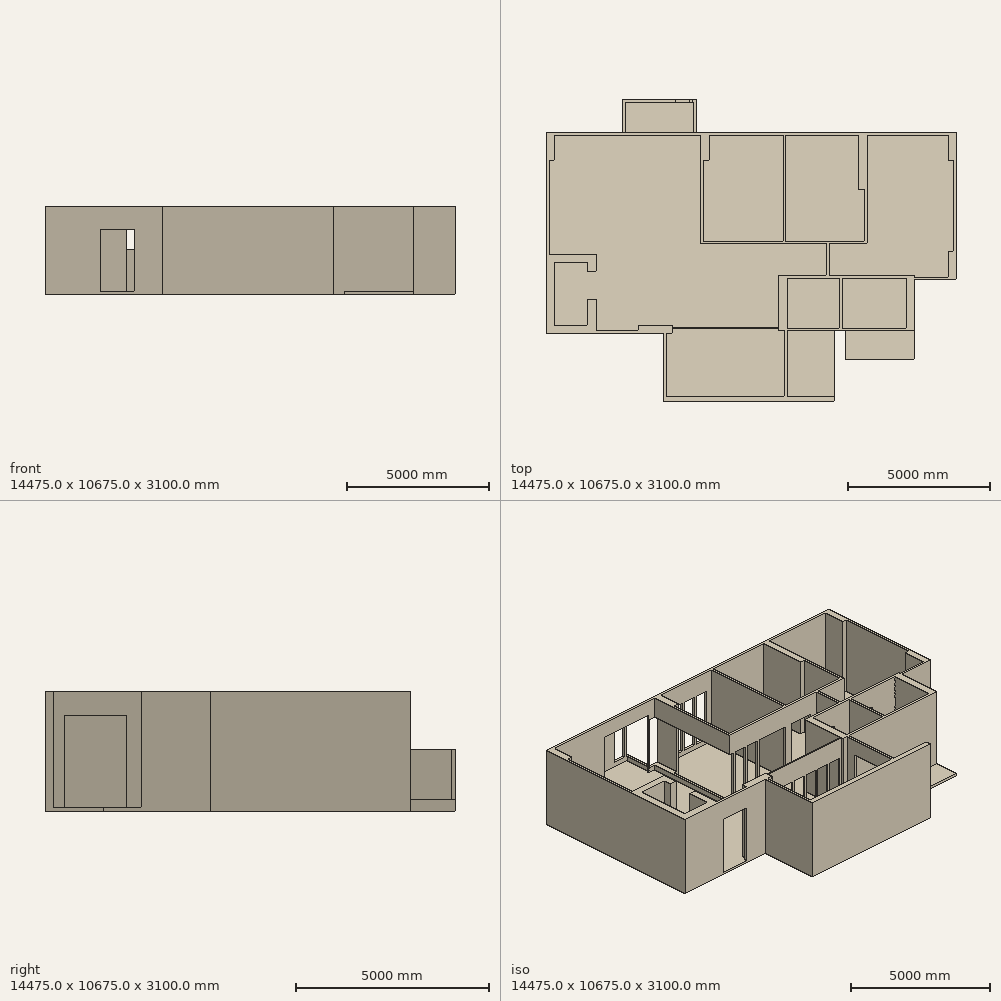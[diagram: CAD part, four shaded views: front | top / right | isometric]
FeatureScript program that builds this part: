
annotation { "Feature Type Name" : "Feature", "Feature Type Description" : "" }
export const myFeature = defineFeature(function(context is Context, id is Id, definition is map)
    precondition{}
    {
        {
            var Q0;
            Q0=qCreatedBy(makeId("Top.planeOp"),FACE);
            var sketch = newSketch(context, id + "F0", { "sketchPlane" : qUnion([Q0])});
            skLineSegment(sketch, "E0", {"start": v(0, 0) * mm, "end": v(-4125, 0) * mm});
            skLineSegment(sketch, "E1", {"start": v(-4125, 0) * mm, "end": v(-4125, 7100) * mm});
            skLineSegment(sketch, "E2", {"start": v(-4125, 7100) * mm, "end": v(-1425, 7100) * mm});
            skLineSegment(sketch, "E3", {"start": v(-1425, 7100) * mm, "end": v(-1425, 8275) * mm});
            skLineSegment(sketch, "E4", {"start": v(-1425, 8275) * mm, "end": v(1175, 8275) * mm});
            skLineSegment(sketch, "E5", {"start": v(1175, 8275) * mm, "end": v(1175, 7100) * mm});
            skLineSegment(sketch, "E6", {"start": v(1175, 7100) * mm, "end": v(10350, 7100) * mm});
            skLineSegment(sketch, "E7", {"start": v(10350, 7100) * mm, "end": v(10350, 1900) * mm});
            skLineSegment(sketch, "E8", {"start": v(10350, 1900) * mm, "end": v(8875, 1900) * mm});
            skLineSegment(sketch, "E9", {"start": v(8875, 1900) * mm, "end": v(8875, -900) * mm});
            skLineSegment(sketch, "E10", {"start": v(8875, -900) * mm, "end": v(6425, -900) * mm});
            skLineSegment(sketch, "E11", {"start": v(6050, -900) * mm, "end": v(6050, -2400) * mm});
            skLineSegment(sketch, "E12", {"start": v(6050, -2400) * mm, "end": v(0, -2400) * mm});
            skLineSegment(sketch, "E13", {"start": v(0, -2400) * mm, "end": v(0, 0) * mm});
            skLineSegment(sketch, "E14", {"start": v(6425, -900) * mm, "end": v(6425, 0) * mm});
            skLineSegment(sketch, "E15", {"start": v(6050, 0) * mm, "end": v(6050, -900) * mm});
            skLineSegment(sketch, "E16", {"start": v(6050, 0) * mm, "end": v(6050, 100) * mm});
            skLineSegment(sketch, "E17", {"start": v(6050, 100) * mm, "end": v(6425, 100) * mm});
            skLineSegment(sketch, "E18", {"start": v(6425, 100) * mm, "end": v(6425, 0) * mm});
            skSolve(sketch);
        }
        {
            var Q0;
            Q0=qSketchRegion(id+"F0",true);
            extrude(context, id + "F1", {"entities" : qUnion([Q0]), "oppositeDirection" : true, "depth" : 100 * mm});
        }
        {
            var Q0;
            Q0=makeQuery(id+"F1.opExtrude","CAP_FACE",FACE,{"disambiguationData":[OSD([sQuery(id+"F0.wireOp",EDGE,"E0"),sQuery(id+"F0.wireOp",EDGE,"E1"),sQuery(id+"F0.wireOp",EDGE,"E2"),sQuery(id+"F0.wireOp",EDGE,"E3"),sQuery(id+"F0.wireOp",EDGE,"E4"),sQuery(id+"F0.wireOp",EDGE,"E5"),sQuery(id+"F0.wireOp",EDGE,"E6"),sQuery(id+"F0.wireOp",EDGE,"E7"),sQuery(id+"F0.wireOp",EDGE,"E8"),sQuery(id+"F0.wireOp",EDGE,"E9"),sQuery(id+"F0.wireOp",EDGE,"E10"),sQuery(id+"F0.wireOp",EDGE,"E11"),sQuery(id+"F0.wireOp",EDGE,"E12"),sQuery(id+"F0.wireOp",EDGE,"E13"),sQuery(id+"F0.wireOp",EDGE,"E14"),sQuery(id+"F0.wireOp",EDGE,"EO6Hl1aY-iN83-L0no-XnAw-wlp1sX6jhs91"),sQuery(id+"F0.wireOp",EDGE,"E15")])],"isStart":true});
            var sketch = newSketch(context, id + "F2", { "sketchPlane" : qUnion([Q0])});
            skLineSegment(sketch, "E19", {"start": v(-4125, 0) * mm, "end": v(-4125, 2800) * mm});
            skLineSegment(sketch, "E20", {"start": v(-4125, 2800) * mm, "end": v(-2375, 2800) * mm});
            skLineSegment(sketch, "E21", {"start": v(-2375, 2800) * mm, "end": v(-2375, 2200) * mm});
            skLineSegment(sketch, "E22", {"start": v(-2375, 2200) * mm, "end": v(-2675, 2200) * mm});
            skLineSegment(sketch, "E23", {"start": v(-2675, 2200) * mm, "end": v(-2675, 2500) * mm});
            skLineSegment(sketch, "E24", {"start": v(-2675, 2500) * mm, "end": v(-3825, 2500) * mm});
            skLineSegment(sketch, "E25", {"start": v(-3825, 2500) * mm, "end": v(-3825, 300) * mm});
            skLineSegment(sketch, "E26", {"start": v(-3825, 300) * mm, "end": v(-2675, 300) * mm});
            skLineSegment(sketch, "E27", {"start": v(-2675, 300) * mm, "end": v(-2675, 1200) * mm});
            skLineSegment(sketch, "E28", {"start": v(-2675, 1200) * mm, "end": v(-2375, 1200) * mm});
            skLineSegment(sketch, "E29", {"start": v(-2375, 1200) * mm, "end": v(-2375, 0) * mm});
            skLineSegment(sketch, "E30", {"start": v(-2375, 0) * mm, "end": v(-4125, 0) * mm});
            skSolve(sketch);
        }
        {
            var Q0;
            Q0=qSketchRegion(id+"F2",true);
            extrude(context, id + "F3", {"entities" : qUnion([Q0]), "operationType" : NewBodyOperationType.ADD, "depth" : 3000 * mm});
        }
        {
            var Q0;
            Q0=makeQuery(id+"F1.opExtrude","CAP_FACE",FACE,{"disambiguationData":[OSD([sQuery(id+"F0.wireOp",EDGE,"E0"),sQuery(id+"F0.wireOp",EDGE,"E1"),sQuery(id+"F0.wireOp",EDGE,"E2"),sQuery(id+"F0.wireOp",EDGE,"E3"),sQuery(id+"F0.wireOp",EDGE,"E4"),sQuery(id+"F0.wireOp",EDGE,"E5"),sQuery(id+"F0.wireOp",EDGE,"E6"),sQuery(id+"F0.wireOp",EDGE,"E7"),sQuery(id+"F0.wireOp",EDGE,"E8"),sQuery(id+"F0.wireOp",EDGE,"E9"),sQuery(id+"F0.wireOp",EDGE,"E10"),sQuery(id+"F0.wireOp",EDGE,"E11"),sQuery(id+"F0.wireOp",EDGE,"E12"),sQuery(id+"F0.wireOp",EDGE,"E13"),sQuery(id+"F0.wireOp",EDGE,"E14"),sQuery(id+"F0.wireOp",EDGE,"EO6Hl1aY-iN83-L0no-XnAw-wlp1sX6jhs91"),sQuery(id+"F0.wireOp",EDGE,"E15")])],"isStart":true});
            var sketch = newSketch(context, id + "F4", { "sketchPlane" : qUnion([Q0])});
            skLineSegment(sketch, "E31.bottom", {"start": v(-4125, 7100) * mm, "end": v(-3825, 7100) * mm});
            skLineSegment(sketch, "E31.top", {"start": v(-4125, 6100) * mm, "end": v(-3825, 6100) * mm});
            skLineSegment(sketch, "E31.left", {"start": v(-4125, 7100) * mm, "end": v(-4125, 6100) * mm});
            skLineSegment(sketch, "E31.right", {"start": v(-3825, 7100) * mm, "end": v(-3825, 6100) * mm});
            skLineSegment(sketch, "E32.bottom", {"start": v(1325, 7100) * mm, "end": v(1625, 7100) * mm});
            skLineSegment(sketch, "E32.top", {"start": v(1325, 6100) * mm, "end": v(1625, 6100) * mm});
            skLineSegment(sketch, "E32.left", {"start": v(1325, 7100) * mm, "end": v(1325, 6100) * mm});
            skLineSegment(sketch, "E32.right", {"start": v(1625, 7100) * mm, "end": v(1625, 6100) * mm});
            skLineSegment(sketch, "E33.bottom", {"start": v(6900, 7100) * mm, "end": v(7200, 7100) * mm});
            skLineSegment(sketch, "E33.top", {"start": v(6900, 5100) * mm, "end": v(7200, 5100) * mm});
            skLineSegment(sketch, "E33.left", {"start": v(6900, 7100) * mm, "end": v(6900, 5100) * mm});
            skLineSegment(sketch, "E33.right", {"start": v(7200, 7100) * mm, "end": v(7200, 5100) * mm});
            skLineSegment(sketch, "E34.bottom", {"start": v(10350, 7100) * mm, "end": v(10050, 7100) * mm});
            skLineSegment(sketch, "E34.top", {"start": v(10350, 6100) * mm, "end": v(10050, 6100) * mm});
            skLineSegment(sketch, "E34.left", {"start": v(10350, 7100) * mm, "end": v(10350, 6100) * mm});
            skLineSegment(sketch, "E34.right", {"start": v(10050, 7100) * mm, "end": v(10050, 6100) * mm});
            skLineSegment(sketch, "E35.bottom", {"start": v(10350, 1900) * mm, "end": v(10050, 1900) * mm});
            skLineSegment(sketch, "E35.top", {"start": v(10350, 2900) * mm, "end": v(10050, 2900) * mm});
            skLineSegment(sketch, "E35.left", {"start": v(10350, 1900) * mm, "end": v(10350, 2900) * mm});
            skLineSegment(sketch, "E35.right", {"start": v(10050, 1900) * mm, "end": v(10050, 2900) * mm});
            skLineSegment(sketch, "E36.bottom", {"start": v(8875, 2050) * mm, "end": v(8575, 2050) * mm});
            skLineSegment(sketch, "E36.top", {"start": v(8875, 100) * mm, "end": v(8575, 100) * mm});
            skLineSegment(sketch, "E36.left", {"start": v(8875, 2050) * mm, "end": v(8875, 100) * mm});
            skLineSegment(sketch, "E36.right", {"start": v(8575, 2050) * mm, "end": v(8575, 100) * mm});
            skLineSegment(sketch, "E37.bottom", {"start": v(4375, 2050) * mm, "end": v(4075, 2050) * mm});
            skLineSegment(sketch, "E37.top", {"start": v(4375, 100) * mm, "end": v(4075, 100) * mm});
            skLineSegment(sketch, "E37.left", {"start": v(4375, 2050) * mm, "end": v(4375, 100) * mm});
            skLineSegment(sketch, "E37.right", {"start": v(4075, 2050) * mm, "end": v(4075, 100) * mm});
            skLineSegment(sketch, "E38.bottom", {"start": v(325, 0) * mm, "end": v(-875, 0) * mm});
            skLineSegment(sketch, "E38.top", {"start": v(325, 300) * mm, "end": v(-875, 300) * mm});
            skLineSegment(sketch, "E38.left", {"start": v(325, 0) * mm, "end": v(325, 300) * mm});
            skLineSegment(sketch, "E38.right", {"start": v(-875, 0) * mm, "end": v(-875, 300) * mm});
            skLineSegment(sketch, "E39.bottom", {"start": v(0, -2400) * mm, "end": v(6050, -2400) * mm});
            skLineSegment(sketch, "E39.top", {"start": v(0, -2200) * mm, "end": v(6050, -2200) * mm});
            skLineSegment(sketch, "E39.left", {"start": v(0, -2400) * mm, "end": v(0, -2200) * mm});
            skLineSegment(sketch, "E39.right", {"start": v(6050, -2400) * mm, "end": v(6050, -2200) * mm});
            skSolve(sketch);
        }
        {
            var Q0;
            Q0=qSketchRegion(id+"F4",true);
            extrude(context, id + "F5", {"entities" : qUnion([Q0]), "operationType" : NewBodyOperationType.ADD, "depth" : 3000 * mm});
        }
        {
            var Q0;
            Q0=makeQuery(id+"F1.opExtrude","CAP_FACE",FACE,{"disambiguationData":[OSD([sQuery(id+"F0.wireOp",EDGE,"E0"),sQuery(id+"F0.wireOp",EDGE,"E1"),sQuery(id+"F0.wireOp",EDGE,"E2"),sQuery(id+"F0.wireOp",EDGE,"E3"),sQuery(id+"F0.wireOp",EDGE,"E4"),sQuery(id+"F0.wireOp",EDGE,"E5"),sQuery(id+"F0.wireOp",EDGE,"E6"),sQuery(id+"F0.wireOp",EDGE,"E7"),sQuery(id+"F0.wireOp",EDGE,"E8"),sQuery(id+"F0.wireOp",EDGE,"E9"),sQuery(id+"F0.wireOp",EDGE,"E10"),sQuery(id+"F0.wireOp",EDGE,"E11"),sQuery(id+"F0.wireOp",EDGE,"E12"),sQuery(id+"F0.wireOp",EDGE,"E13"),sQuery(id+"F0.wireOp",EDGE,"E14"),sQuery(id+"F0.wireOp",EDGE,"EO6Hl1aY-iN83-L0no-XnAw-wlp1sX6jhs91"),sQuery(id+"F0.wireOp",EDGE,"E15")])],"isStart":true});
            var sketch = newSketch(context, id + "F6", { "sketchPlane" : qUnion([Q0])});
            skLineSegment(sketch, "E40", {"start": v(0, -2200) * mm, "end": v(0, 0) * mm});
            skLineSegment(sketch, "E41", {"start": v(0, 0) * mm, "end": v(-4125, 0) * mm});
            skLineSegment(sketch, "E42", {"start": v(-4125, 0) * mm, "end": v(-4125, 7100) * mm});
            skLineSegment(sketch, "E43", {"start": v(-4125, 7100) * mm, "end": v(-1425, 7100) * mm});
            skLineSegment(sketch, "E44", {"start": v(-1425, 7100) * mm, "end": v(-1425, 7000) * mm});
            skLineSegment(sketch, "E45", {"start": v(-1425, 7000) * mm, "end": v(-4025, 7000) * mm});
            skLineSegment(sketch, "E46", {"start": v(-4025, 7000) * mm, "end": v(-4025, 100) * mm});
            skLineSegment(sketch, "E47", {"start": v(-4025, 100) * mm, "end": v(100, 100) * mm});
            skLineSegment(sketch, "E48", {"start": v(100, 100) * mm, "end": v(100, -2200) * mm});
            skLineSegment(sketch, "E49", {"start": v(100, -2200) * mm, "end": v(0, -2200) * mm});
            skLineSegment(sketch, "E50.bottom", {"start": v(-1425, 7100) * mm, "end": v(1325, 7100) * mm});
            skLineSegment(sketch, "E50.top", {"start": v(-1425, 7000) * mm, "end": v(1325, 7000) * mm});
            skLineSegment(sketch, "E50.right", {"start": v(1325, 7100) * mm, "end": v(1325, 7000) * mm});
            skSolve(sketch);
        }
        {
            var Q0;
            Q0=qSketchRegion(id+"F6",true);
            extrude(context, id + "F7", {"entities" : qUnion([Q0]), "depth" : 3000 * mm});
        }
        {
            var Q0;
            Q0=makeQuery(id+"F1.opExtrude","CAP_FACE",FACE,{"disambiguationData":[OSD([sQuery(id+"F0.wireOp",EDGE,"E0"),sQuery(id+"F0.wireOp",EDGE,"E1"),sQuery(id+"F0.wireOp",EDGE,"E2"),sQuery(id+"F0.wireOp",EDGE,"E3"),sQuery(id+"F0.wireOp",EDGE,"E4"),sQuery(id+"F0.wireOp",EDGE,"E5"),sQuery(id+"F0.wireOp",EDGE,"E6"),sQuery(id+"F0.wireOp",EDGE,"E7"),sQuery(id+"F0.wireOp",EDGE,"E8"),sQuery(id+"F0.wireOp",EDGE,"E9"),sQuery(id+"F0.wireOp",EDGE,"E10"),sQuery(id+"F0.wireOp",EDGE,"E11"),sQuery(id+"F0.wireOp",EDGE,"E12"),sQuery(id+"F0.wireOp",EDGE,"E13"),sQuery(id+"F0.wireOp",EDGE,"E14"),sQuery(id+"F0.wireOp",EDGE,"EO6Hl1aY-iN83-L0no-XnAw-wlp1sX6jhs91"),sQuery(id+"F0.wireOp",EDGE,"E15")])],"isStart":true});
            var sketch = newSketch(context, id + "F8", { "sketchPlane" : qUnion([Q0])});
            skLineSegment(sketch, "E51", {"start": v(7200, 3170) * mm, "end": v(7200, 7100) * mm});
            skLineSegment(sketch, "E52", {"start": v(7200, 7100) * mm, "end": v(1325, 7100) * mm});
            skLineSegment(sketch, "E53", {"start": v(1325, 7100) * mm, "end": v(1325, 3170) * mm});
            skLineSegment(sketch, "E54", {"start": v(1325, 3170) * mm, "end": v(5775, 3170) * mm});
            skLineSegment(sketch, "E55.bottom", {"start": v(1425, 3270) * mm, "end": v(4225, 3270) * mm});
            skLineSegment(sketch, "E55.top", {"start": v(1425, 7000) * mm, "end": v(4225, 7000) * mm});
            skLineSegment(sketch, "E55.left", {"start": v(1425, 3270) * mm, "end": v(1425, 7000) * mm});
            skLineSegment(sketch, "E55.right", {"start": v(4225, 3270) * mm, "end": v(4225, 7000) * mm});
            skLineSegment(sketch, "E56.bottom", {"start": v(4325, 7000) * mm, "end": v(7100, 7000) * mm});
            skLineSegment(sketch, "E56.top", {"start": v(4325, 3270) * mm, "end": v(7100, 3270) * mm});
            skLineSegment(sketch, "E56.left", {"start": v(4325, 7000) * mm, "end": v(4325, 3270) * mm});
            skLineSegment(sketch, "E56.right", {"start": v(7100, 7000) * mm, "end": v(7100, 3270) * mm});
            skLineSegment(sketch, "E57.bottom", {"start": v(7200, 7100) * mm, "end": v(10350, 7100) * mm});
            skLineSegment(sketch, "E57.top", {"start": v(7200, 7000) * mm, "end": v(10250, 7000) * mm});
            skLineSegment(sketch, "E57.left", {"start": v(7200, 7100) * mm, "end": v(7200, 7000) * mm});
            skLineSegment(sketch, "E57.right", {"start": v(10350, 7100) * mm, "end": v(10350, 7000) * mm});
            skLineSegment(sketch, "E58.bottom", {"start": v(10350, 7100) * mm, "end": v(10250, 7100) * mm});
            skLineSegment(sketch, "E58.top", {"start": v(10350, 1900) * mm, "end": v(10250, 1900) * mm});
            skLineSegment(sketch, "E58.left", {"start": v(10350, 7100) * mm, "end": v(10350, 1900) * mm});
            skLineSegment(sketch, "E58.right", {"start": v(10250, 7000) * mm, "end": v(10250, 1975) * mm});
            skPoint(sketch, "E59.oppositeSnap0", {"position": v(8875, 1975) * mm});
            skLineSegment(sketch, "E59.bottom", {"start": v(10250, 1900) * mm, "end": v(8875, 1900) * mm});
            skLineSegment(sketch, "E59.top", {"start": v(10250, 1975) * mm, "end": v(8875, 1975) * mm});
            skLineSegment(sketch, "E59.right", {"start": v(8875, 1900) * mm, "end": v(8875, 1975) * mm});
            skLineSegment(sketch, "E60.bottom", {"start": v(8575, 2050) * mm, "end": v(5875, 2050) * mm});
            skLineSegment(sketch, "E60.top", {"start": v(8575, 1950) * mm, "end": v(6325, 1950) * mm});
            skLineSegment(sketch, "E60.left", {"start": v(8575, 2050) * mm, "end": v(8575, 1950) * mm});
            skLineSegment(sketch, "E60.right", {"start": v(4375, 2050) * mm, "end": v(4375, 1950) * mm});
            skLineSegment(sketch, "E61.bottom", {"start": v(4375, 100) * mm, "end": v(8575, 100) * mm});
            skLineSegment(sketch, "E61.top", {"start": v(4375, 200) * mm, "end": v(6225, 200) * mm});
            skLineSegment(sketch, "E61.left", {"start": v(4375, 100) * mm, "end": v(4375, 200) * mm});
            skLineSegment(sketch, "E61.right", {"start": v(8575, 100) * mm, "end": v(8575, 200) * mm});
            skLineSegment(sketch, "E62.left", {"start": v(6225, 1950) * mm, "end": v(6225, 200) * mm});
            skLineSegment(sketch, "E62.right", {"start": v(6325, 1950) * mm, "end": v(6325, 200) * mm});
            skLineSegment(sketch, "E63.trimOffspring", {"start": v(6225, 1950) * mm, "end": v(4375, 1950) * mm});
            skLineSegment(sketch, "E64.trimOffspring", {"start": v(6325, 200) * mm, "end": v(8575, 200) * mm});
            skLineSegment(sketch, "E65.left", {"start": v(5775, 3170) * mm, "end": v(5775, 2050) * mm});
            skLineSegment(sketch, "E65.right", {"start": v(5875, 3170) * mm, "end": v(5875, 2050) * mm});
            skLineSegment(sketch, "E66.trimOffspring", {"start": v(5875, 3170) * mm, "end": v(7200, 3170) * mm});
            skLineSegment(sketch, "E67.trimOffspring", {"start": v(5775, 2050) * mm, "end": v(4375, 2050) * mm});
            skLineSegment(sketch, "E68.bottom", {"start": v(4375, 200) * mm, "end": v(4275, 200) * mm});
            skLineSegment(sketch, "E68.top", {"start": v(4375, -2400) * mm, "end": v(4275, -2400) * mm});
            skLineSegment(sketch, "E68.left", {"start": v(4375, 200) * mm, "end": v(4375, -2400) * mm});
            skLineSegment(sketch, "E68.right", {"start": v(4275, 200) * mm, "end": v(4275, -2400) * mm});
            skSolve(sketch);
        }
        {
            var Q0;
            Q0=qSketchRegion(id+"F8",true);
            extrude(context, id + "F9", {"entities" : qUnion([Q0]), "operationType" : NewBodyOperationType.ADD, "depth" : 3000 * mm});
        }
        {
            var Q0;
            Q0=makeQuery(id+"F7.opExtrude","SWEPT_FACE",FACE,{"disambiguationData":[OSD([sQuery(id+"F6.wireOp",EDGE,"E41")])]});
            var sketch = newSketch(context, id + "F10", { "sketchPlane" : qUnion([Q0])});
            skLineSegment(sketch, "E69.bottom", {"start": v(-975, 0) * mm, "end": v(-2175, 0) * mm});
            skLineSegment(sketch, "E69.top", {"start": v(-975, 2200) * mm, "end": v(-2175, 2200) * mm});
            skLineSegment(sketch, "E69.left", {"start": v(-975, 0) * mm, "end": v(-975, 2200) * mm});
            skLineSegment(sketch, "E69.right", {"start": v(-2175, 0) * mm, "end": v(-2175, 2200) * mm});
            skSolve(sketch);
        }
        {
            var Q0;
            Q0=qSketchRegion(id+"F10",true);
            extrude(context, id + "F11", {"entities" : qUnion([Q0]), "operationType" : NewBodyOperationType.REMOVE, "oppositeDirection" : true, "depth" : 100 * mm});
        }
        {
            var Q0;
            Q0=makeQuery(id+"F9.opExtrude","SWEPT_FACE",FACE,{"disambiguationData":[OSD([sQuery(id+"F8.wireOp",EDGE,"E54")])]});
            var sketch = newSketch(context, id + "F12", { "sketchPlane" : qUnion([Q0])});
            skLineSegment(sketch, "E70.bottom", {"start": v(3175, 2200) * mm, "end": v(4175, 2200) * mm});
            skLineSegment(sketch, "E70.top", {"start": v(3175, 0) * mm, "end": v(4175, 0) * mm});
            skLineSegment(sketch, "E70.left", {"start": v(3175, 2200) * mm, "end": v(3175, 0) * mm});
            skLineSegment(sketch, "E70.right", {"start": v(4175, 2200) * mm, "end": v(4175, 0) * mm});
            skLineSegment(sketch, "E71.bottom", {"start": v(4475, 2200) * mm, "end": v(5475, 2200) * mm});
            skLineSegment(sketch, "E71.top", {"start": v(4475, 0) * mm, "end": v(5475, 0) * mm});
            skLineSegment(sketch, "E71.left", {"start": v(4475, 2200) * mm, "end": v(4475, 0) * mm});
            skLineSegment(sketch, "E71.right", {"start": v(5475, 2200) * mm, "end": v(5475, 0) * mm});
            skSolve(sketch);
        }
        {
            var Q0;
            Q0=qSketchRegion(id+"F12",true);
            extrude(context, id + "F13", {"entities" : qUnion([Q0]), "operationType" : NewBodyOperationType.REMOVE, "oppositeDirection" : true, "depth" : 100 * mm});
        }
        {
            var Q0;
            Q0=makeQuery(id+"F9.opExtrude","SWEPT_FACE",FACE,{"disambiguationData":[OSD([sQuery(id+"F8.wireOp",EDGE,"E65.left")])]});
            var sketch = newSketch(context, id + "F14", { "sketchPlane" : qUnion([Q0])});
            skLineSegment(sketch, "E72.bottom", {"start": v(-3110, 2200) * mm, "end": v(-2110, 2200) * mm});
            skLineSegment(sketch, "E72.top", {"start": v(-3110, 0) * mm, "end": v(-2110, 0) * mm});
            skLineSegment(sketch, "E72.left", {"start": v(-3110, 2200) * mm, "end": v(-3110, 0) * mm});
            skLineSegment(sketch, "E72.right", {"start": v(-2110, 2200) * mm, "end": v(-2110, 0) * mm});
            skSolve(sketch);
        }
        {
            var Q0;
            Q0=qSketchRegion(id+"F14",true);
            extrude(context, id + "F15", {"entities" : qUnion([Q0]), "operationType" : NewBodyOperationType.REMOVE, "oppositeDirection" : true, "depth" : 100 * mm});
        }
        {
            var Q0;
            Q0=makeQuery(id+"F9.opExtrude","SWEPT_FACE",FACE,{"disambiguationData":[OSD([sQuery(id+"F8.wireOp",EDGE,"E67.trimOffspring")])]});
            var sketch = newSketch(context, id + "F16", { "sketchPlane" : qUnion([Q0])});
            skLineSegment(sketch, "E73.bottom", {"start": v(-5475, 2200) * mm, "end": v(-4475, 2200) * mm});
            skLineSegment(sketch, "E73.top", {"start": v(-5475, 0) * mm, "end": v(-4475, 0) * mm});
            skLineSegment(sketch, "E73.left", {"start": v(-5475, 2200) * mm, "end": v(-5475, 0) * mm});
            skLineSegment(sketch, "E73.right", {"start": v(-4475, 2200) * mm, "end": v(-4475, 0) * mm});
            skPoint(sketch, "E74.oppositeSnap0", {"position": v(-5075, 0) * mm});
            skLineSegment(sketch, "E74.bottom", {"start": v(-6425, 2200) * mm, "end": v(-7425, 2200) * mm});
            skLineSegment(sketch, "E74.top", {"start": v(-6425, 0) * mm, "end": v(-7425, 0) * mm});
            skLineSegment(sketch, "E74.left", {"start": v(-6425, 2200) * mm, "end": v(-6425, 0) * mm});
            skLineSegment(sketch, "E74.right", {"start": v(-7425, 2200) * mm, "end": v(-7425, 0) * mm});
            skSolve(sketch);
        }
        {
            var Q0;
            Q0=qSketchRegion(id+"F16",true);
            extrude(context, id + "F17", {"entities" : qUnion([Q0]), "operationType" : NewBodyOperationType.REMOVE, "oppositeDirection" : true, "depth" : 100 * mm});
        }
        {
            var Q0;
            Q0=makeQuery(id+"F9.opExtrude","SWEPT_FACE",FACE,{"disambiguationData":[OSD([sQuery(id+"F8.wireOp",EDGE,"E68.right")])]});
            var sketch = newSketch(context, id + "F18", { "sketchPlane" : qUnion([Q0])});
            skLineSegment(sketch, "E75.bottom", {"start": v(300, 2400) * mm, "end": v(1900, 2400) * mm});
            skLineSegment(sketch, "E75.top", {"start": v(300, 0) * mm, "end": v(1900, 0) * mm});
            skLineSegment(sketch, "E75.left", {"start": v(300, 2400) * mm, "end": v(300, 0) * mm});
            skLineSegment(sketch, "E75.right", {"start": v(1900, 2400) * mm, "end": v(1900, 0) * mm});
            skSolve(sketch);
        }
        {
            var Q0;
            Q0=qSketchRegion(id+"F18",true);
            extrude(context, id + "F19", {"entities" : qUnion([Q0]), "operationType" : NewBodyOperationType.REMOVE, "oppositeDirection" : true, "depth" : 100 * mm});
        }
        {
            var Q0;
            Q0=makeQuery(id+"F7.opExtrude","SWEPT_FACE",FACE,{"disambiguationData":[OSD([sQuery(id+"F6.wireOp",EDGE,"E45"),sQuery(id+"F6.wireOp",EDGE,"E50.top")])]});
            var sketch = newSketch(context, id + "F20", { "sketchPlane" : qUnion([Q0])});
            skLineSegment(sketch, "E76.bottom", {"start": v(-1275, 2400) * mm, "end": v(1025, 2400) * mm});
            skLineSegment(sketch, "E76.top", {"start": v(-1275, 0) * mm, "end": v(1025, 0) * mm});
            skLineSegment(sketch, "E76.left", {"start": v(-1275, 2400) * mm, "end": v(-1275, 0) * mm});
            skLineSegment(sketch, "E76.right", {"start": v(1025, 2400) * mm, "end": v(1025, 0) * mm});
            skSolve(sketch);
        }
        {
            var Q0;
            Q0=qSketchRegion(id+"F20",true);
            extrude(context, id + "F21", {"entities" : qUnion([Q0]), "operationType" : NewBodyOperationType.REMOVE, "oppositeDirection" : true, "depth" : 100 * mm});
        }
        {
            var Q0;
            Q0=makeQuery(id+"F1.opExtrude","CAP_FACE",FACE,{"disambiguationData":[OSD([sQuery(id+"F0.wireOp",EDGE,"E0"),sQuery(id+"F0.wireOp",EDGE,"E1"),sQuery(id+"F0.wireOp",EDGE,"E2"),sQuery(id+"F0.wireOp",EDGE,"E3"),sQuery(id+"F0.wireOp",EDGE,"E4"),sQuery(id+"F0.wireOp",EDGE,"E5"),sQuery(id+"F0.wireOp",EDGE,"E6"),sQuery(id+"F0.wireOp",EDGE,"E7"),sQuery(id+"F0.wireOp",EDGE,"E8"),sQuery(id+"F0.wireOp",EDGE,"E9"),sQuery(id+"F0.wireOp",EDGE,"E10"),sQuery(id+"F0.wireOp",EDGE,"E11"),sQuery(id+"F0.wireOp",EDGE,"E12"),sQuery(id+"F0.wireOp",EDGE,"E13"),sQuery(id+"F0.wireOp",EDGE,"E14"),sQuery(id+"F0.wireOp",EDGE,"E15"),sQuery(id+"F0.wireOp",EDGE,"E16"),sQuery(id+"F0.wireOp",EDGE,"E17"),sQuery(id+"F0.wireOp",EDGE,"E18")])],"isStart":true});
            var sketch = newSketch(context, id + "F22", { "sketchPlane" : qUnion([Q0])});
            skLineSegment(sketch, "E77.bottom", {"start": v(6050, -2200) * mm, "end": v(5950, -2200) * mm});
            skLineSegment(sketch, "E77.top", {"start": v(6050, 100) * mm, "end": v(5950, 100) * mm});
            skLineSegment(sketch, "E77.left", {"start": v(6050, -2200) * mm, "end": v(6050, 100) * mm});
            skLineSegment(sketch, "E77.right", {"start": v(5950, -2200) * mm, "end": v(5950, 100) * mm});
            skLineSegment(sketch, "E78", {"start": v(-1425, 7100) * mm, "end": v(-1425, 8275) * mm});
            skLineSegment(sketch, "E79", {"start": v(-1425, 8275) * mm, "end": v(1175, 8275) * mm});
            skLineSegment(sketch, "E80", {"start": v(1175, 8275) * mm, "end": v(1175, 7100) * mm});
            skLineSegment(sketch, "E81", {"start": v(1175, 7100) * mm, "end": v(1075, 7100) * mm});
            skLineSegment(sketch, "E82", {"start": v(1075, 7100) * mm, "end": v(1075, 8175) * mm});
            skLineSegment(sketch, "E83", {"start": v(1075, 8175) * mm, "end": v(-1325, 8175) * mm});
            skLineSegment(sketch, "E84", {"start": v(-1325, 8175) * mm, "end": v(-1325, 7100) * mm});
            skLineSegment(sketch, "E85", {"start": v(-1325, 7100) * mm, "end": v(-1425, 7100) * mm});
            skSolve(sketch);
        }
        {
            var Q0;
            Q0=makeQuery(id+"F22.imprint","IMPRINT",FACE,{"disambiguationData":[TD([[makeQuery(id+"F22.imprint","IMPRINT",EDGE,{"derivedFrom":sQuery(id+"F22.wireOp",EDGE,"E78")}),-1.0]])]});
            var Q1;
            Q1=makeQuery(id+"F22.imprint","IMPRINT",FACE,{"disambiguationData":[TD([[makeQuery(id+"F22.imprint","IMPRINT",EDGE,{"derivedFrom":sQuery(id+"F22.wireOp",EDGE,"E77.bottom")}),1.0]])]});
            extrude(context, id + "F23", {"entities" : qUnion([Q0, Q1]), "operationType" : NewBodyOperationType.ADD, "depth" : 1500 * mm});
        }
        {
            var Q0;
            Q0=makeQuery(id+"F1.opExtrude","CAP_FACE",FACE,{"disambiguationData":[OSD([sQuery(id+"F0.wireOp",EDGE,"E0"),sQuery(id+"F0.wireOp",EDGE,"E1"),sQuery(id+"F0.wireOp",EDGE,"E2"),sQuery(id+"F0.wireOp",EDGE,"E3"),sQuery(id+"F0.wireOp",EDGE,"E4"),sQuery(id+"F0.wireOp",EDGE,"E5"),sQuery(id+"F0.wireOp",EDGE,"E6"),sQuery(id+"F0.wireOp",EDGE,"E7"),sQuery(id+"F0.wireOp",EDGE,"E8"),sQuery(id+"F0.wireOp",EDGE,"E9"),sQuery(id+"F0.wireOp",EDGE,"E10"),sQuery(id+"F0.wireOp",EDGE,"E11"),sQuery(id+"F0.wireOp",EDGE,"E12"),sQuery(id+"F0.wireOp",EDGE,"E13"),sQuery(id+"F0.wireOp",EDGE,"E14"),sQuery(id+"F0.wireOp",EDGE,"E15"),sQuery(id+"F0.wireOp",EDGE,"E16"),sQuery(id+"F0.wireOp",EDGE,"E17"),sQuery(id+"F0.wireOp",EDGE,"E18")])],"isStart":true});
            var sketch = newSketch(context, id + "F24", { "sketchPlane" : qUnion([Q0])});
            skLineSegment(sketch, "E86.bottom", {"start": v(325, 225) * mm, "end": v(4075, 225) * mm});
            skLineSegment(sketch, "E86.top", {"start": v(325, 175) * mm, "end": v(4075, 175) * mm});
            skLineSegment(sketch, "E86.left", {"start": v(325, 225) * mm, "end": v(325, 175) * mm});
            skLineSegment(sketch, "E86.right", {"start": v(4075, 225) * mm, "end": v(4075, 175) * mm});
            skSolve(sketch);
        }
        {
            var Q0;
            Q0=qSketchRegion(id+"F24",true);
            extrude(context, id + "F25", {"entities" : qUnion([Q0]), "depth" : 3000 * mm});
        }
        {
            var Q0;
            Q0=makeQuery(id+"F25.opExtrude","SWEPT_FACE",FACE,{"disambiguationData":[OSD([sQuery(id+"F24.wireOp",EDGE,"E86.top")])]});
            var sketch = newSketch(context, id + "F26", { "sketchPlane" : qUnion([Q0])});
            skLineSegment(sketch, "E87.bottom", {"start": v(425, 2200) * mm, "end": v(935, 2200) * mm});
            skLineSegment(sketch, "E87.top", {"start": v(425, 200) * mm, "end": v(935, 200) * mm});
            skLineSegment(sketch, "E87.left", {"start": v(425, 2200) * mm, "end": v(425, 200) * mm});
            skLineSegment(sketch, "E87.right", {"start": v(935, 2200) * mm, "end": v(935, 200) * mm});
            skLineSegment(sketch, "E88.bottom", {"start": v(1035, 2200) * mm, "end": v(1545, 2200) * mm});
            skLineSegment(sketch, "E88.top", {"start": v(1035, 200) * mm, "end": v(1545, 200) * mm});
            skLineSegment(sketch, "E88.left", {"start": v(1035, 2200) * mm, "end": v(1035, 200) * mm});
            skLineSegment(sketch, "E88.right", {"start": v(1545, 2200) * mm, "end": v(1545, 200) * mm});
            skLineSegment(sketch, "E89.bottom", {"start": v(1645, 2200) * mm, "end": v(2150, 2200) * mm});
            skLineSegment(sketch, "E89.top", {"start": v(1645, 200) * mm, "end": v(2150, 200) * mm});
            skLineSegment(sketch, "E89.left", {"start": v(1645, 2200) * mm, "end": v(1645, 200) * mm});
            skLineSegment(sketch, "E89.right", {"start": v(2150, 2200) * mm, "end": v(2150, 200) * mm});
            skLineSegment(sketch, "E90.bottom", {"start": v(3465, 2200) * mm, "end": v(3975, 2200) * mm});
            skLineSegment(sketch, "E90.top", {"start": v(3465, 200) * mm, "end": v(3975, 200) * mm});
            skLineSegment(sketch, "E90.left", {"start": v(3465, 2200) * mm, "end": v(3465, 200) * mm});
            skLineSegment(sketch, "E90.right", {"start": v(3975, 2200) * mm, "end": v(3975, 200) * mm});
            skLineSegment(sketch, "E91.bottom", {"start": v(2250, 2200) * mm, "end": v(2755, 2200) * mm});
            skLineSegment(sketch, "E91.top", {"start": v(2250, 200) * mm, "end": v(2755, 200) * mm});
            skLineSegment(sketch, "E91.left", {"start": v(2250, 2200) * mm, "end": v(2250, 200) * mm});
            skLineSegment(sketch, "E91.right", {"start": v(2755, 2200) * mm, "end": v(2755, 200) * mm});
            skLineSegment(sketch, "E92.bottom", {"start": v(2855, 2200) * mm, "end": v(3365, 2200) * mm});
            skLineSegment(sketch, "E92.top", {"start": v(2855, 200) * mm, "end": v(3365, 200) * mm});
            skLineSegment(sketch, "E92.left", {"start": v(2855, 2200) * mm, "end": v(2855, 200) * mm});
            skLineSegment(sketch, "E92.right", {"start": v(3365, 2200) * mm, "end": v(3365, 200) * mm});
            skSolve(sketch);
        }
        {
            var Q0;
            Q0=qSketchRegion(id+"F26",true);
            extrude(context, id + "F27", {"entities" : qUnion([Q0]), "operationType" : NewBodyOperationType.REMOVE, "endBound" : BoundingType.THROUGH_ALL, "oppositeDirection" : true, "depth" : 25 * mm});
        }
    });
